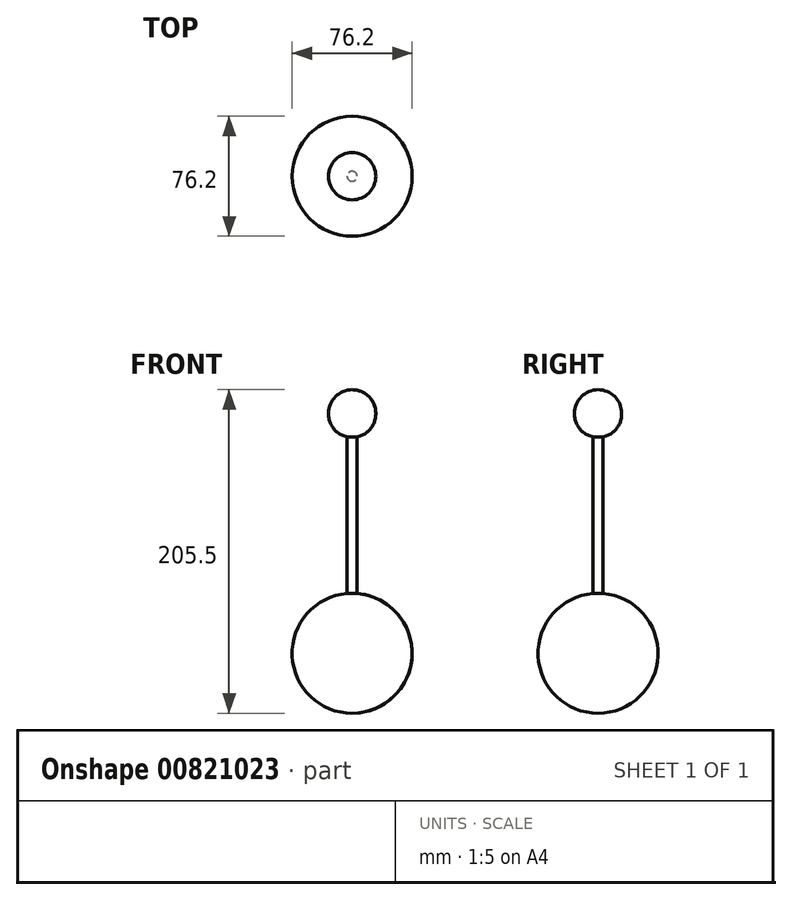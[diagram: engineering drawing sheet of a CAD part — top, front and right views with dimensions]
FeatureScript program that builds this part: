
annotation { "Feature Type Name" : "Feature", "Feature Type Description" : "" }
export const myFeature = defineFeature(function(context is Context, id is Id, definition is map)
    precondition{}
    {
        {
            var Q0;
            Q0=qCreatedBy(makeId("Top.planeOp"),FACE);
            var sketch = newSketch(context, id + "F0", { "sketchPlane" : qUnion([Q0])});
            skCircle(sketch, "E0", {"center": v(0, 0) * mm, "radius": 38.1 * mm});
            skSolve(sketch);
        }
        {
            var Q0;
            Q0 = qSketchRegion(id + "F0", true);
            extrude(context, id + "F1", {"entities" : qUnion([Q0]), "depth" : 38.1 * mm, "offsetDistance" : 25.4 * mm, "hasSecondDirection" : true, "secondDirectionOppositeDirection" : true, "secondDirectionDepth" : 38.1 * mm});
        }
        {
            var Q0;
            Q0=makeQuery(id+"F1.opExtrude","CAP_FACE",FACE,{"disambiguationData":[OSD([sQuery(id+"F0.wireOp",EDGE,"E0")])],"isStart":false});
            fillet(context, id + "F2", {"entities" : qUnion([Q0]), "radius" : 38.1 * mm, "tangentPropagation" : true, "allowEdgeOverflow" : false});
        }
        {
            var Q0;
            Q0=makeQuery(id+"F1.opExtrude","CAP_EDGE",EDGE,{"disambiguationData":[OSD([sQuery(id+"F0.wireOp",EDGE,"E0")])],"isStart":true});
            fillet(context, id + "F3", {"entities" : qUnion([Q0]), "radius" : 38.1 * mm, "tangentPropagation" : true, "allowEdgeOverflow" : false});
        }
        {
            var Q0;
            Q0=qCreatedBy(makeId("Top.planeOp"),FACE);
            var sketch = newSketch(context, id + "F4", { "sketchPlane" : qUnion([Q0])});
            skCircle(sketch, "E1", {"center": v(0, 0) * mm, "radius": 3.17 * mm});
            skSolve(sketch);
        }
        {
            var Q0;
            Q0 = qSketchRegion(id + "F4", true);
            extrude(context, id + "F5", {"entities" : qUnion([Q0]), "operationType" : NewBodyOperationType.ADD, "depth" : 152.4 * mm, "offsetDistance" : 25.4 * mm});
        }
        {
            var Q0;
            Q0=makeQuery(id+"F5.opExtrude","CAP_FACE",FACE,{"disambiguationData":[OSD([sQuery(id+"F4.wireOp",EDGE,"E1")])],"isStart":false});
            var sketch = newSketch(context, id + "F6", { "sketchPlane" : qUnion([Q0])});
            skCircle(sketch, "E2", {"center": v(0, 0) * mm, "radius": 15 * mm});
            skSolve(sketch);
        }
        {
            var Q0;
            Q0 = qSketchRegion(id + "F6", true);
            extrude(context, id + "F7", {"entities" : qUnion([Q0]), "operationType" : NewBodyOperationType.ADD, "depth" : 15 * mm, "offsetDistance" : 25 * mm, "hasSecondDirection" : true, "secondDirectionOppositeDirection" : true, "secondDirectionDepth" : 15 * mm});
        }
        {
            var Q0;
            Q0=makeQuery(id+"F7.opExtrude","CAP_FACE",FACE,{"disambiguationData":[OSD([sQuery(id+"F6.wireOp",EDGE,"E2")])],"isStart":false});
            fillet(context, id + "F8", {"entities" : qUnion([Q0]), "radius" : 15 * mm, "tangentPropagation" : true, "allowEdgeOverflow" : false});
        }
        {
            var Q0;
            Q0=makeQuery(id+"F7.opExtrude","CAP_EDGE",EDGE,{"disambiguationData":[OSD([sQuery(id+"F6.wireOp",EDGE,"E2")])],"isStart":true});
            fillet(context, id + "F9", {"entities" : qUnion([Q0]), "radius" : 15 * mm, "tangentPropagation" : true, "allowEdgeOverflow" : false});
        }
        {
            var Q0;
            Q0=qCreatedBy(makeId("Front.planeOp"),FACE);
            var sketch = newSketch(context, id + "F10", { "sketchPlane" : qUnion([Q0])});
            skCircle(sketch, "E3", {"center": v(0, 0) * mm, "radius": 153.05 * mm});
            skSolve(sketch);
        }
        {
            var Q0;
            Q0=makeQuery(id+"F10.imprint","IMPRINT",FACE,{"disambiguationData":[TD([[makeQuery(id+"F10.imprint","IMPRINT",EDGE,{"derivedFrom":sQuery(id+"F10.wireOp",EDGE,"E3")}),1.0]])]});
            var Q1;
            Q1=sQuery(id+"F10.wireOp",EDGE,"E3");
            extrude(context, id + "F11", {"entities" : qUnion([Q0]), "bodyType" : ToolBodyType.SURFACE, "operationType" : NewBodyOperationType.REMOVE, "surfaceEntities" : qUnion([Q1]), "endBound" : BoundingType.SYMMETRIC, "depth" : 6 * mm, "offsetDistance" : 25 * mm});
        }
    });
